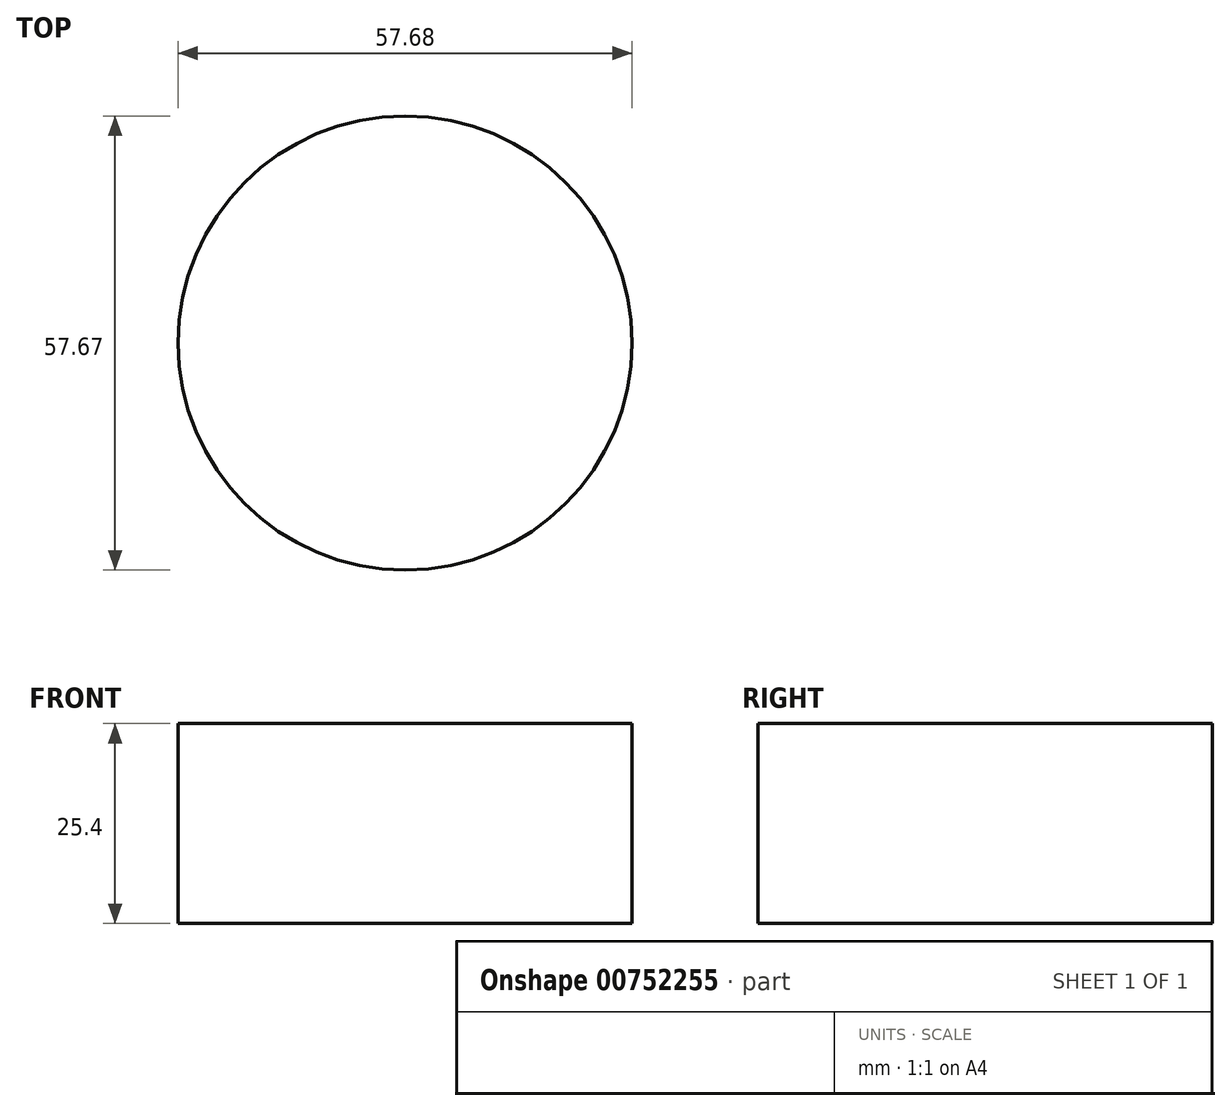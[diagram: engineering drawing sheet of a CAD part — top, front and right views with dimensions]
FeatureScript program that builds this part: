
annotation { "Feature Type Name" : "Feature", "Feature Type Description" : "" }
export const myFeature = defineFeature(function(context is Context, id is Id, definition is map)
    precondition{}
    {
        {
            var Q0;
            Q0=qCreatedBy(makeId("Top.planeOp"),FACE);
            var sketch = newSketch(context, id + "F0", { "sketchPlane" : qUnion([Q0])});
            skCircle(sketch, "E0", {"center": v(0, -12.65) * mm, "radius": 28.84 * mm});
            skSolve(sketch);
        }
        {
            var Q0;
            Q0=makeQuery(id+"F0.imprint","IMPRINT",FACE,{"disambiguationData":[TD([[makeQuery(id+"F0.imprint","IMPRINT",EDGE,{"derivedFrom":sQuery(id+"F0.wireOp",EDGE,"E0")}),1.0]])]});
            extrude(context, id + "F1", {"entities" : qUnion([Q0]), "depth" : 25.4 * mm, "offsetDistance" : 25.4 * mm});
        }
    });
